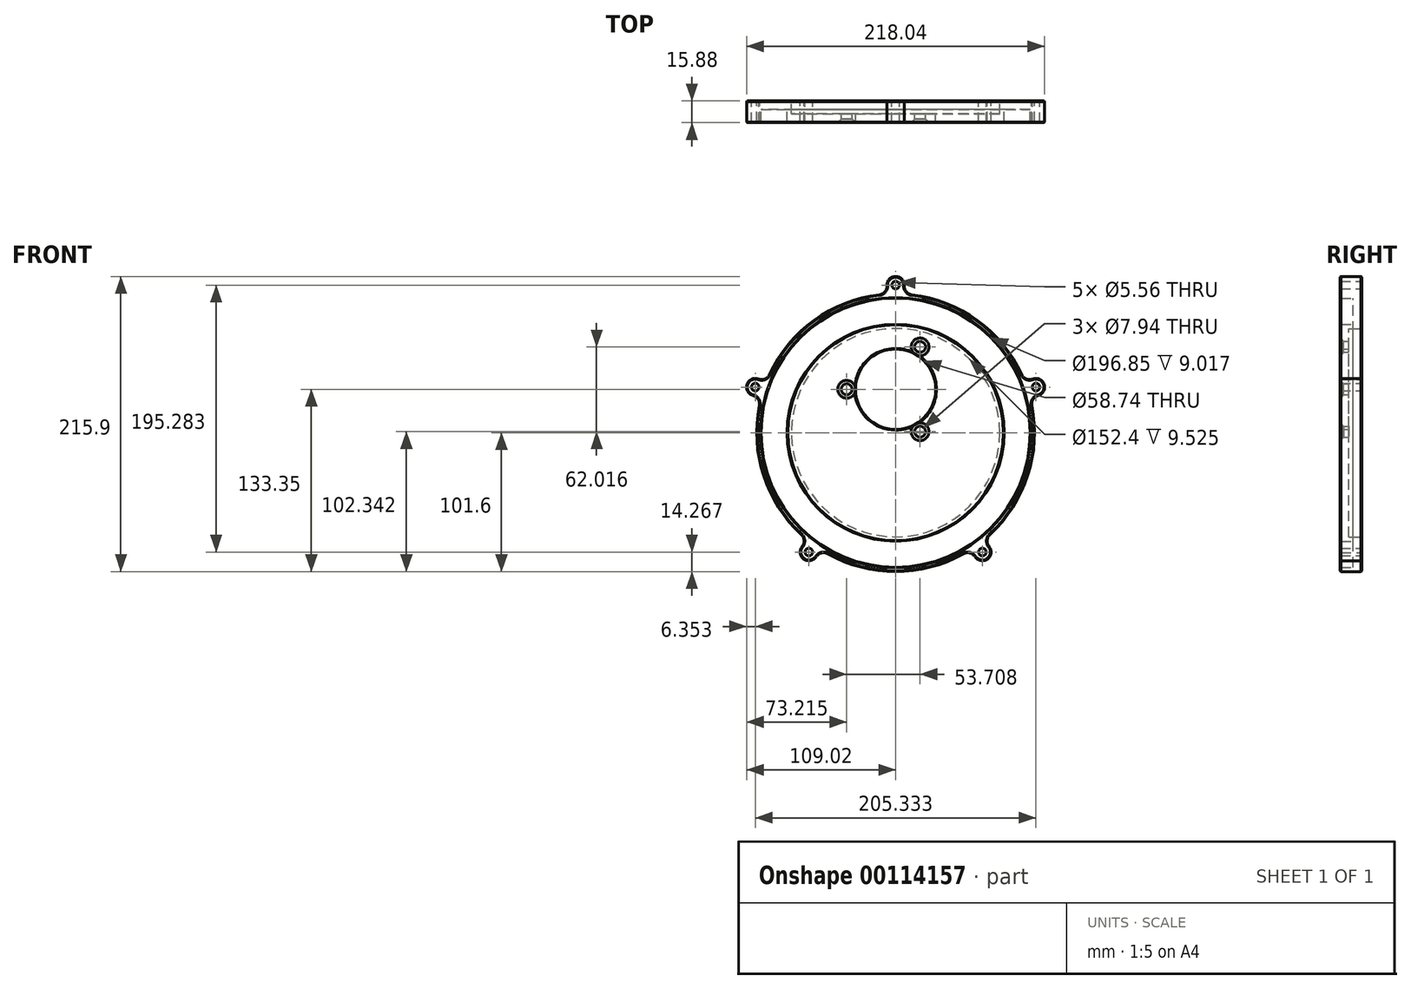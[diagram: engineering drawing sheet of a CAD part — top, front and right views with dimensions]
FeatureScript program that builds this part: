
annotation { "Feature Type Name" : "Feature", "Feature Type Description" : "" }
export const myFeature = defineFeature(function(context is Context, id is Id, definition is map)
    precondition{}
    {
        {
            var Q0;
            Q0=qCreatedBy(makeId("Front.planeOp"),FACE);
            var sketch = newSketch(context, id + "F0", { "sketchPlane" : qUnion([Q0])});
            skCircle(sketch, "E0", {"center": v(0, 0) * mm, "radius": 101.6 * mm});
            skCircle(sketch, "E1", {"center": v(0, 0) * mm, "radius": 98.43 * mm});
            skCircle(sketch, "E2", {"center": v(0, 0) * mm, "radius": 79.38 * mm});
            skCircle(sketch, "E3", {"center": v(0, 31.75) * mm, "radius": 29.37 * mm});
            skCircle(sketch, "E4", {"center": v(-35.8, 31.75) * mm, "radius": 3.97 * mm});
            skCircle(sketch, "E5.1.0", {"center": v(17.9, 0.74) * mm, "radius": 3.97 * mm});
            skCircle(sketch, "E5.2.0", {"center": v(17.9, 62.76) * mm, "radius": 3.97 * mm});
            skCircle(sketch, "E6", {"center": v(0, 107.95) * mm, "radius": 6.35 * mm});
            skLineSegment(sketch, "E7", {"start": v(-6.35, 107.95) * mm, "end": v(-6.35, 101.4) * mm});
            skLineSegment(sketch, "E8", {"start": v(6.35, 107.95) * mm, "end": v(6.35, 101.4) * mm});
            skCircle(sketch, "E9", {"center": v(0, 107.95) * mm, "radius": 2.78 * mm});
            skCircle(sketch, "E10.1.0", {"center": v(-102.67, 33.36) * mm, "radius": 6.35 * mm});
            skCircle(sketch, "E10.1.1", {"center": v(-102.67, 33.36) * mm, "radius": 2.78 * mm});
            skLineSegment(sketch, "E10.1.2", {"start": v(-100.7, 39.4) * mm, "end": v(-94.48, 37.37) * mm});
            skLineSegment(sketch, "E10.1.3", {"start": v(-104.63, 27.32) * mm, "end": v(-98.4, 25.3) * mm});
            skCircle(sketch, "E10.2.0", {"center": v(-63.45, -87.33) * mm, "radius": 6.35 * mm});
            skCircle(sketch, "E10.2.1", {"center": v(-63.45, -87.33) * mm, "radius": 2.78 * mm});
            skLineSegment(sketch, "E10.2.2", {"start": v(-68.59, -83.6) * mm, "end": v(-64.74, -78.3) * mm});
            skLineSegment(sketch, "E10.2.3", {"start": v(-58.31, -91.07) * mm, "end": v(-54.46, -85.77) * mm});
            skCircle(sketch, "E10.3.0", {"center": v(63.45, -87.33) * mm, "radius": 6.35 * mm});
            skCircle(sketch, "E10.3.1", {"center": v(63.45, -87.33) * mm, "radius": 2.78 * mm});
            skLineSegment(sketch, "E10.3.2", {"start": v(58.31, -91.07) * mm, "end": v(54.46, -85.77) * mm});
            skLineSegment(sketch, "E10.3.3", {"start": v(68.59, -83.6) * mm, "end": v(64.74, -78.3) * mm});
            skCircle(sketch, "E10.4.0", {"center": v(102.67, 33.36) * mm, "radius": 6.35 * mm});
            skCircle(sketch, "E10.4.1", {"center": v(102.67, 33.36) * mm, "radius": 2.78 * mm});
            skLineSegment(sketch, "E10.4.2", {"start": v(104.63, 27.32) * mm, "end": v(98.4, 25.3) * mm});
            skLineSegment(sketch, "E10.4.3", {"start": v(100.7, 39.4) * mm, "end": v(94.48, 37.37) * mm});
            skSolve(sketch);
        }
        {
            var Q0;
            {var subQ0=sQuery(id+"F0.wireOp",EDGE,"E10.2.3");Q0=makeQuery(id+"F0.imprint","IMPRINT",FACE,{"disambiguationData":[TD([[makeQuery(id+"F0.imprint","IMPRINT",EDGE,{"derivedFrom":subQ0}),1.0]])]});}
            var Q1;
            {var subQ0=sQuery(id+"F0.wireOp",EDGE,"E10.2.2");Q1=makeQuery(id+"F0.imprint","IMPRINT",FACE,{"disambiguationData":[TD([[makeQuery(id+"F0.imprint","IMPRINT",EDGE,{"derivedFrom":subQ0}),-1.0]])]});}
            var Q2;
            Q2=makeQuery(id+"F0.imprint","IMPRINT",FACE,{"disambiguationData":[TD([[makeQuery(id+"F0.imprint","IMPRINT",EDGE,{"derivedFrom":sQuery(id+"F0.wireOp",EDGE,"E10.2.1")}),-1.0]])]});
            var Q3;
            {var subQ0=sQuery(id+"F0.wireOp",EDGE,"E10.3.3");Q3=makeQuery(id+"F0.imprint","IMPRINT",FACE,{"disambiguationData":[TD([[makeQuery(id+"F0.imprint","IMPRINT",EDGE,{"derivedFrom":subQ0}),1.0]])]});}
            var Q4;
            {var subQ0=sQuery(id+"F0.wireOp",EDGE,"E10.3.2");Q4=makeQuery(id+"F0.imprint","IMPRINT",FACE,{"disambiguationData":[TD([[makeQuery(id+"F0.imprint","IMPRINT",EDGE,{"derivedFrom":subQ0}),-1.0]])]});}
            var Q5;
            Q5=makeQuery(id+"F0.imprint","IMPRINT",FACE,{"disambiguationData":[TD([[makeQuery(id+"F0.imprint","IMPRINT",EDGE,{"derivedFrom":sQuery(id+"F0.wireOp",EDGE,"E10.3.1")}),-1.0]])]});
            var Q6;
            {var subQ0=sQuery(id+"F0.wireOp",EDGE,"E10.4.3");Q6=makeQuery(id+"F0.imprint","IMPRINT",FACE,{"disambiguationData":[TD([[makeQuery(id+"F0.imprint","IMPRINT",EDGE,{"derivedFrom":subQ0}),1.0]])]});}
            var Q7;
            {var subQ0=sQuery(id+"F0.wireOp",EDGE,"E10.4.2");Q7=makeQuery(id+"F0.imprint","IMPRINT",FACE,{"disambiguationData":[TD([[makeQuery(id+"F0.imprint","IMPRINT",EDGE,{"derivedFrom":subQ0}),-1.0]])]});}
            var Q8;
            Q8=makeQuery(id+"F0.imprint","IMPRINT",FACE,{"disambiguationData":[TD([[makeQuery(id+"F0.imprint","IMPRINT",EDGE,{"derivedFrom":sQuery(id+"F0.wireOp",EDGE,"E10.4.1")}),-1.0]])]});
            var Q9;
            {var subQ0=sQuery(id+"F0.wireOp",EDGE,"E8");Q9=makeQuery(id+"F0.imprint","IMPRINT",FACE,{"disambiguationData":[TD([[makeQuery(id+"F0.imprint","IMPRINT",EDGE,{"derivedFrom":subQ0}),-1.0]])]});}
            var Q10;
            {var subQ0=sQuery(id+"F0.wireOp",EDGE,"E7");Q10=makeQuery(id+"F0.imprint","IMPRINT",FACE,{"disambiguationData":[TD([[makeQuery(id+"F0.imprint","IMPRINT",EDGE,{"derivedFrom":subQ0}),1.0]])]});}
            var Q11;
            Q11=makeQuery(id+"F0.imprint","IMPRINT",FACE,{"disambiguationData":[TD([[makeQuery(id+"F0.imprint","IMPRINT",EDGE,{"derivedFrom":sQuery(id+"F0.wireOp",EDGE,"E9")}),-1.0]])]});
            var Q12;
            {var subQ0=sQuery(id+"F0.wireOp",EDGE,"E10.1.2");Q12=makeQuery(id+"F0.imprint","IMPRINT",FACE,{"disambiguationData":[TD([[makeQuery(id+"F0.imprint","IMPRINT",EDGE,{"derivedFrom":subQ0}),-1.0]])]});}
            var Q13;
            {var subQ0=sQuery(id+"F0.wireOp",EDGE,"E10.1.3");Q13=makeQuery(id+"F0.imprint","IMPRINT",FACE,{"disambiguationData":[TD([[makeQuery(id+"F0.imprint","IMPRINT",EDGE,{"derivedFrom":subQ0}),1.0]])]});}
            var Q14;
            Q14=makeQuery(id+"F0.imprint","IMPRINT",FACE,{"disambiguationData":[TD([[makeQuery(id+"F0.imprint","IMPRINT",EDGE,{"derivedFrom":sQuery(id+"F0.wireOp",EDGE,"E10.1.1")}),-1.0]])]});
            var Q15;
            Q15=makeQuery(id+"F0.imprint","IMPRINT",FACE,{"disambiguationData":[TD([[makeQuery(id+"F0.imprint","IMPRINT",EDGE,{"derivedFrom":sQuery(id+"F0.wireOp",EDGE,"E1")}),-1.0]])]});
            var Q16;
            Q16=makeQuery(id+"F0.imprint","IMPRINT",FACE,{"disambiguationData":[TD([[makeQuery(id+"F0.imprint","IMPRINT",EDGE,{"derivedFrom":sQuery(id+"F0.wireOp",EDGE,"E2")}),1.0]])]});
            extrude(context, id + "F1", {"entities" : qUnion([Q0, Q1, Q2, Q3, Q4, Q5, Q6, Q7, Q8, Q9, Q10, Q11, Q12, Q13, Q14, Q15, Q16]), "depth" : 15.88 * mm});
        }
        {
            var Q0;
            Q0=makeQuery(id+"F0.imprint","IMPRINT",FACE,{"disambiguationData":[TD([[makeQuery(id+"F0.imprint","IMPRINT",EDGE,{"derivedFrom":sQuery(id+"F0.wireOp",EDGE,"E1")}),1.0]])]});
            extrude(context, id + "F2", {"entities" : qUnion([Q0]), "operationType" : NewBodyOperationType.ADD, "depth" : 6.35 * mm});
        }
        {
            var Q0;
            Q0=makeQuery(id+"F0.imprint","IMPRINT",FACE,{"disambiguationData":[TD([[makeQuery(id+"F0.imprint","IMPRINT",EDGE,{"derivedFrom":sQuery(id+"F0.wireOp",EDGE,"E2")}),1.0]])]});
            var sketch = newSketch(context, id + "F3", { "sketchPlane" : qUnion([Q0])});
            skCircle(sketch, "E11", {"center": v(0, 0) * mm, "radius": 76.2 * mm});
            skSolve(sketch);
        }
        {
            var Q0;
            Q0=makeQuery(id+"F3.imprint","IMPRINT",FACE,{"disambiguationData":[TD([[makeQuery(id+"F3.imprint","IMPRINT",EDGE,{"derivedFrom":sQuery(id+"F3.wireOp",EDGE,"E11")}),1.0]])]});
            extrude(context, id + "F4", {"entities" : qUnion([Q0]), "operationType" : NewBodyOperationType.REMOVE, "depth" : 9.52 * mm});
        }
        {
            var Q0;
            Q0=makeQuery(id+"F1.opExtrude","SWEPT_EDGE",EDGE,{"disambiguationData":[OSD([sQuery(id+"F0.wireOp",EDGE,"E0"),sQuery(id+"F0.wireOp",EDGE,"E8")])]});
            var Q1;
            Q1=makeQuery(id+"F1.opExtrude","SWEPT_EDGE",EDGE,{"disambiguationData":[OSD([sQuery(id+"F0.wireOp",EDGE,"E0"),sQuery(id+"F0.wireOp",EDGE,"E10.4.3")])]});
            var Q2;
            Q2=makeQuery(id+"F1.opExtrude","SWEPT_EDGE",EDGE,{"disambiguationData":[OSD([sQuery(id+"F0.wireOp",EDGE,"E0"),sQuery(id+"F0.wireOp",EDGE,"E10.3.3")])]});
            var Q3;
            Q3=makeQuery(id+"F1.opExtrude","SWEPT_EDGE",EDGE,{"disambiguationData":[OSD([sQuery(id+"F0.wireOp",EDGE,"E0"),sQuery(id+"F0.wireOp",EDGE,"E10.3.2")])]});
            var Q4;
            Q4=makeQuery(id+"F1.opExtrude","SWEPT_EDGE",EDGE,{"disambiguationData":[OSD([sQuery(id+"F0.wireOp",EDGE,"E0"),sQuery(id+"F0.wireOp",EDGE,"E10.2.3")])]});
            var Q5;
            Q5=makeQuery(id+"F1.opExtrude","SWEPT_EDGE",EDGE,{"disambiguationData":[OSD([sQuery(id+"F0.wireOp",EDGE,"E0"),sQuery(id+"F0.wireOp",EDGE,"E10.2.2")])]});
            var Q6;
            Q6=makeQuery(id+"F1.opExtrude","SWEPT_EDGE",EDGE,{"disambiguationData":[OSD([sQuery(id+"F0.wireOp",EDGE,"E0"),sQuery(id+"F0.wireOp",EDGE,"E10.1.3")])]});
            var Q7;
            Q7=makeQuery(id+"F1.opExtrude","SWEPT_EDGE",EDGE,{"disambiguationData":[OSD([sQuery(id+"F0.wireOp",EDGE,"E0"),sQuery(id+"F0.wireOp",EDGE,"E10.1.2")])]});
            var Q8;
            Q8=makeQuery(id+"F1.opExtrude","SWEPT_EDGE",EDGE,{"disambiguationData":[OSD([sQuery(id+"F0.wireOp",EDGE,"E0"),sQuery(id+"F0.wireOp",EDGE,"E7")])]});
            var Q9;
            Q9=makeQuery(id+"F1.opExtrude","SWEPT_EDGE",EDGE,{"disambiguationData":[OSD([sQuery(id+"F0.wireOp",EDGE,"E0"),sQuery(id+"F0.wireOp",EDGE,"E10.4.2")])]});
            fillet(context, id + "F5", {"entities" : qUnion([Q0, Q1, Q2, Q3, Q4, Q5, Q6, Q7, Q8, Q9]), "radius" : 6.35 * mm, "tangentPropagation" : true, "allowEdgeOverflow" : false});
        }
        {
            var Q0;
            Q0=makeQuery(id+"F1.opExtrude","CAP_EDGE",EDGE,{"disambiguationData":[OSD([sQuery(id+"F0.wireOp",EDGE,"E5.2.0")])],"isStart":false});
            var Q1;
            Q1=makeQuery(id+"F1.opExtrude","CAP_EDGE",EDGE,{"disambiguationData":[OSD([sQuery(id+"F0.wireOp",EDGE,"E5.1.0")])],"isStart":false});
            var Q2;
            Q2=makeQuery(id+"F1.opExtrude","CAP_EDGE",EDGE,{"disambiguationData":[OSD([sQuery(id+"F0.wireOp",EDGE,"E4")])],"isStart":false});
            chamfer(context, id + "F6", {"entities" : qUnion([Q0, Q1, Q2]), "width" : 2.54 * mm, "tangentPropagation" : true});
        }
        {
            var Q0;
            {var subQ0=sQuery(id+"F0.wireOp",EDGE,"E0");Q0=makeQuery(id+"F1.opExtrude","CAP_EDGE",EDGE,{"disambiguationData":[OSD([subQ0]),TDD([makeQuery(id+"F0.imprint","IMPRINT",EDGE,{"disambiguationData":[TD([[makeQuery(id+"F0.imprint","INTERSECT",VERTEX,{"derivedFrom":[subQ0,sQuery(id+"F0.wireOp",EDGE,"E8")]}),1.0]])],"derivedFrom":subQ0})])],"isStart":false});}
            var Q1;
            Q1=makeQuery(id+"F1.opExtrude","CAP_EDGE",EDGE,{"disambiguationData":[OSD([sQuery(id+"F0.wireOp",EDGE,"E2")])],"isStart":false});
            var Q2;
            Q2=makeQuery(id+"F1.opExtrude","CAP_EDGE",EDGE,{"disambiguationData":[OSD([sQuery(id+"F0.wireOp",EDGE,"E1")])],"isStart":false});
            var Q3;
            Q3=makeQuery(id+"F1.opExtrude","CAP_EDGE",EDGE,{"disambiguationData":[OSD([sQuery(id+"F0.wireOp",EDGE,"E3")])],"isStart":false});
            var Q4;
            Q4=makeQuery(id+"F4.boolean.opBoolean","COPY",EDGE,{"derivedFrom":makeQuery(id+"F4.opExtrude","CAP_EDGE",EDGE,{"disambiguationData":[OSD([sQuery(id+"F0.wireOp",EDGE,"E3")])],"isStart":false})});
            var Q5;
            Q5=makeQuery(id+"F4.boolean.opBoolean","COPY",EDGE,{"derivedFrom":makeQuery(id+"F4.opExtrude","CAP_EDGE",EDGE,{"disambiguationData":[OSD([sQuery(id+"F3.wireOp",EDGE,"E11")])],"isStart":true})});
            var Q6;
            {var subQ0=sQuery(id+"F0.wireOp",EDGE,"E0");Q6=makeQuery(id+"F1.opExtrude","CAP_EDGE",EDGE,{"disambiguationData":[OSD([subQ0]),TDD([makeQuery(id+"F0.imprint","IMPRINT",EDGE,{"disambiguationData":[TD([[makeQuery(id+"F0.imprint","INTERSECT",VERTEX,{"derivedFrom":[subQ0,sQuery(id+"F0.wireOp",EDGE,"E7")]}),-1.0]])],"derivedFrom":subQ0})])],"isStart":true});}
            var Q7;
            Q7=makeQuery(id+"F4.boolean.opBoolean","COPY",EDGE,{"derivedFrom":makeQuery(id+"F4.opExtrude","CAP_EDGE",EDGE,{"disambiguationData":[OSD([sQuery(id+"F0.wireOp",EDGE,"E5.2.0")])],"isStart":false})});
            var Q8;
            Q8=makeQuery(id+"F4.boolean.opBoolean","COPY",EDGE,{"derivedFrom":makeQuery(id+"F4.opExtrude","CAP_EDGE",EDGE,{"disambiguationData":[OSD([sQuery(id+"F0.wireOp",EDGE,"E4")])],"isStart":false})});
            var Q9;
            Q9=makeQuery(id+"F4.boolean.opBoolean","COPY",EDGE,{"derivedFrom":makeQuery(id+"F4.opExtrude","CAP_EDGE",EDGE,{"disambiguationData":[OSD([sQuery(id+"F0.wireOp",EDGE,"E5.1.0")])],"isStart":false})});
            chamfer(context, id + "F7", {"entities" : qUnion([Q0, Q1, Q2, Q3, Q4, Q5, Q6, Q7, Q8, Q9]), "width" : 0.5 * mm, "tangentPropagation" : true});
        }
    });
